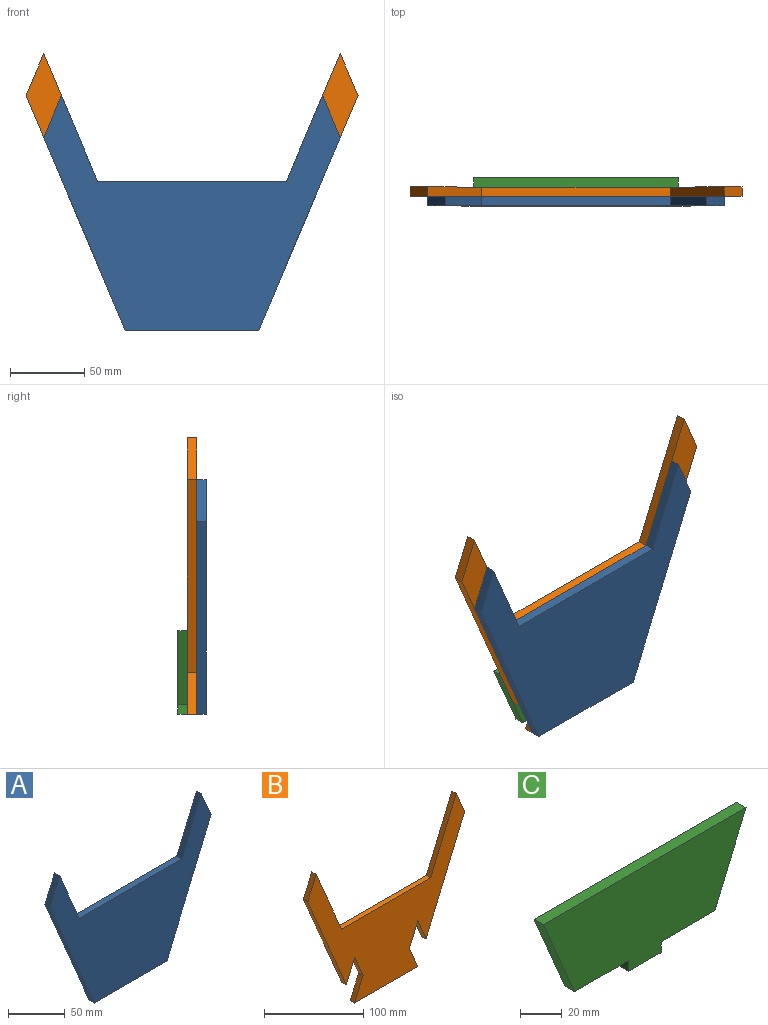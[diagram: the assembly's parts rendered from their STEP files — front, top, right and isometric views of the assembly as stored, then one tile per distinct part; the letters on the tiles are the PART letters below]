
ASSEMBLY  parts=3 mates=2
PART A: 10 faces, bbox 200x6.4x158.2 mm
  f0: plane 28.23x11.94mm, normal (-0.92,0,0.39), area 194.7mm2, adj f1,f7,f8,f9
  f1: plane 130x55mm, normal (-0.92,0,-0.39), area 896.3mm2, adj f0,f2,f8,f9
  f2: plane 90x6.35mm, normal (0,0,-1), area 571.5mm2, adj f1,f3,f8,f9
  f3: plane 130x55mm, normal (0.92,0,-0.39), area 896.3mm2, adj f2,f4,f8,f9
  f4: plane 28.23x11.94mm, normal (0.92,0,0.39), area 194.7mm2, adj f3,f5,f8,f9
  f5: plane 57.74x24.43mm, normal (-0.92,0,0.39), area 398.1mm2, adj f4,f6,f8,f9
  f6: plane 127.26x6.35mm, normal (0,0,1), area 808.1mm2, adj f5,f7,f8,f9
  f7: plane 57.74x24.43mm, normal (0.92,0,0.39), area 398.1mm2, adj f0,f6,f8,f9
  f8: plane 200x158.23mm, normal (0,-1,0), area 15401.2mm2, adj f0,f1,f2,f3,f4,f5,f6,f7
  f9: plane 200x158.23mm, normal (0,1,0), area 15401.2mm2, adj f0,f1,f2,f3,f4,f5,f6,f7
PART B: 16 faces, bbox 223.9x6.4x186.5 mm
  f0: plane 28.23x11.94mm, normal (0.92,0,0.39), area 194.7mm2, adj f1,f13,f14,f15
  f1: plane 85.97x36.37mm, normal (-0.92,0,0.39), area 592.7mm2, adj f0,f2,f14,f15
  f2: plane 127.26x6.35mm, normal (0,0,1), area 808.1mm2, adj f1,f3,f14,f15
  f3: plane 85.97x36.37mm, normal (0.92,0,0.39), area 592.7mm2, adj f2,f4,f14,f15
  f4: plane 28.23x11.94mm, normal (-0.92,0,0.39), area 194.7mm2, adj f3,f5,f14,f15
  f5: plane 130x55mm, normal (-0.92,0,-0.39), area 896.3mm2, adj f4,f6,f14,f15
  f6: plane 28.23x11.94mm, normal (0.92,0,-0.39), area 194.7mm2, adj f5,f7,f14,f15
  f7: plane 28.23x11.94mm, normal (-0.92,0,-0.39), area 194.7mm2, adj f6,f8,f14,f15
  f8: plane 28.23x11.94mm, normal (-0.92,0,0.39), area 194.7mm2, adj f7,f9,f14,f15
  f9: plane 90x6.35mm, normal (0,0,-1), area 571.5mm2, adj f8,f10,f14,f15
  f10: plane 28.23x11.94mm, normal (0.92,0,0.39), area 194.7mm2, adj f9,f11,f14,f15
  f11: plane 28.23x11.94mm, normal (0.92,0,-0.39), area 194.7mm2, adj f10,f12,f14,f15
  f12: plane 28.23x11.94mm, normal (-0.92,0,-0.39), area 194.7mm2, adj f11,f13,f14,f15
  f13: plane 130x55mm, normal (0.92,0,-0.39), area 896.3mm2, adj f0,f12,f14,f15
  f14: plane 223.89x186.46mm, normal (0,1,0), area 15401.2mm2, adj f0,f1,f2,f3,f4,f5,f6,f7
  f15: plane 223.89x186.46mm, normal (0,-1,0), area 15401.2mm2, adj f0,f1,f2,f3,f4,f5,f6,f7
PART C: 10 faces, bbox 137.7x6.4x56.4 mm
  f0: plane 36.61x6.35mm, normal (0,0,-1), area 232.5mm2, adj f1,f7,f8,f9
  f1: plane 6.35x6.35mm, normal (-1,0,0), area 40.3mm2, adj f0,f2,f8,f9
  f2: plane 22.2x6.35mm, normal (0,0,-1), area 141mm2, adj f1,f3,f8,f9
  f3: plane 6.35x6.35mm, normal (1,0,0), area 40.3mm2, adj f2,f4,f8,f9
  f4: plane 36.56x6.35mm, normal (0,0,-1), area 232.2mm2, adj f3,f5,f8,f9
  f5: plane 50x21.15mm, normal (0.92,0,-0.39), area 344.7mm2, adj f4,f6,f8,f9
  f6: plane 137.68x6.35mm, normal (0,0,1), area 874.3mm2, adj f5,f7,f8,f9
  f7: plane 50x21.15mm, normal (-0.92,0,-0.39), area 344.7mm2, adj f0,f6,f8,f9
  f8: plane 137.68x56.35mm, normal (0,1,0), area 5967.3mm2, adj f0,f1,f2,f3,f4,f5,f6,f7
  f9: plane 137.68x56.35mm, normal (0,-1,0), area 5967.3mm2, adj f0,f1,f2,f3,f4,f5,f6,f7
PLACE A at identity
PLACE B t=(0,0,-260)mm
PLACE C t=(-0.03,6.35,0)mm
MATE fastened C.f9 <-> B.f14  axis (0,-1,0) through (0.12,6.35,-129.76)mm
MATE fastened B.f15 <-> A.f9  axis (0,-1,0) through (45.12,0,-129.76)mm
